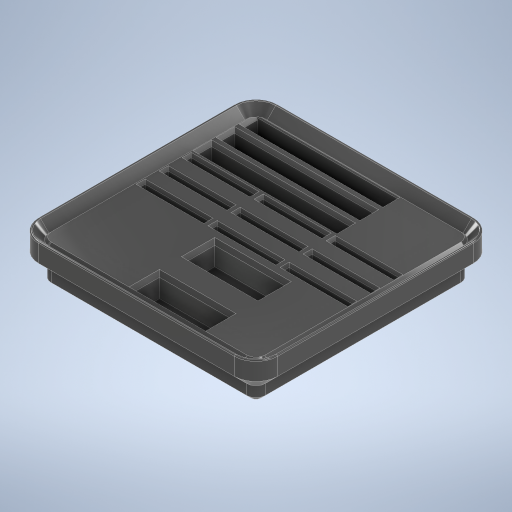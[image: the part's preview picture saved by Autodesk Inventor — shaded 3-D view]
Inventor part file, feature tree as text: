
AUTODESK INVENTOR PART (.ipt)
format: ipt  version: 2023 (Build 270158030, 158C)  size: 650,752 bytes
history: native  units: mm
features: extrude x11, sketch x10, chamfer x8, projected_geometry x6, fillet x1, pattern_linear x1
ambient origin geometry x8: Origin, YZ Plane, XZ Plane, XY Plane, X Axis, Y Axis, Z Axis, Center Point
bodies: Solid2 (feature_tree)
feature tree (37):
  extrude  "base-generic"  Depth=41.5mm
  extrude  "Extrusion8"  Depth=0.1mm TaperAngle=0.0deg
  extrude  "Extrusion9"  Depth=2.15mm
  extrude  "Extrusion10"  Depth=0.8mm
  extrude  "Extrusion11"  Depth=7.75mm
  extrude  "Extrusion12"  Depth=7.75mm
  extrude  "Extrusion15"  Depth=2.4mm TaperAngle=0.0deg
  chamfer  "Chamfer5"  Distance=6.0mm
  fillet  "Fillet4"  Radius=3.75mm
  extrude  "Extrusion16"  Depth=24.0mm
  sketch  "Sketch19"  dims[d79=2.25mm d80=0.0mm d84=1.8mm d85=3.4mm d86=0.0mm d94=1.8mm d95=2.0mm d96=45.0deg d97=0.2mm d98=2.3mm d99=0.0mm d100=4.6mm d101=4.6mm d102=12.1mm d105=11.0mm d106=0.8mm d109=2.25mm d110=24.0mm d111=30.0mm d113=4.0mm d114=30.0mm d116=12.5mm d119=30.0mm d121=4.0mm d122=10.0mm d124=10.0mm d126=2.0mm d127=0.0mm d128=0.4mm d129=2.0mm d130=45.0deg d131=1.8mm d132=0.0mm d133=1.0mm d134=0.5mm d135=5.0mm d136=0.9mm d137=0.4mm d138=2.0mm d139=45.0deg d140=0.1mm d141=2.0mm d142=45.0deg d143=0.6mm d144=2.0mm d145=45.0deg d146=0.2mm d147=2.0mm d148=45.0deg d149=0.5mm d150=2.0mm d151=45.0deg d152=0.5mm d153=2.0mm d154=45.0deg d17=0.5mm d18=0.872665mm d19=0.5mm d20=0.872665mm d24=0.0mm d25=0.0mm d26=0.0mm d27=0.0mm d155=0.0mm]
  extrude  "Extrusion17"  Depth=24.0mm TaperAngle=0.0deg
  chamfer  "Chamfer6"  Distance=1.8mm Angle=45.0deg
  extrude  "Extrusion18"  Depth=24.0mm
  chamfer  "Chamfer7"  Distance=2.3mm
  chamfer  "Chamfer8"  Distance=4.6mm
  chamfer  "Chamfer9"  Distance=4.6mm
  chamfer  "Chamfer10"  Distance=12.1mm
  chamfer  "Chamfer11"  Distance=11.0mm
  chamfer  "Chamfer12"  Distance=0.8mm
  pattern_linear  "Rectangular Pattern1"  Spacing1=2.25mm  [1 undecoded]
  extrude  "Extrusion13"  Depth=24.0mm
  sketch  "Sketch9"  dims[d50=41.5mm d51=41.5mm]
  sketch  "Sketch10"  dims[d52=3.75mm d53=0.1mm d54=0.0mm]
  projected_geometry  "Projected Loop2"
  sketch  "Sketch11"  dims[d55=3.75mm d56=2.15mm d57=-7.853982mm]
  projected_geometry  "Projected Loop3"
  sketch  "Sketch12"  dims[d58=1.8mm d59=0.0mm d60=0.8mm d61=-7.853982mm]
  projected_geometry  "Projected Loop4"
  sketch  "Sketch13"  dims[d62=6.5mm d63=7.75mm]
  sketch  "Sketch14"  dims[d64=7.75mm d65=7.75mm]
  sketch  "Sketch15"  dims[d66=7.75mm d67=2.4mm d68=0.0mm]
  sketch  "Sketch17"  dims[d69=3.0mm d70=6.0mm d71=0.0mm]
  projected_geometry  "Projected Loop6"
  sketch  "Sketch18"  dims[d72=20.0mm d74=42.0mm d75=20.0mm d77=42.0mm d78=3.75mm]
  projected_geometry  "Projected Loop7"
  projected_geometry  "Projected Loop8"
note: 1 required parameter value undecoded (feature->parameter linkage not recoverable at this tier; creation-order binding heuristic only, values carry confidence <= 0.55)
